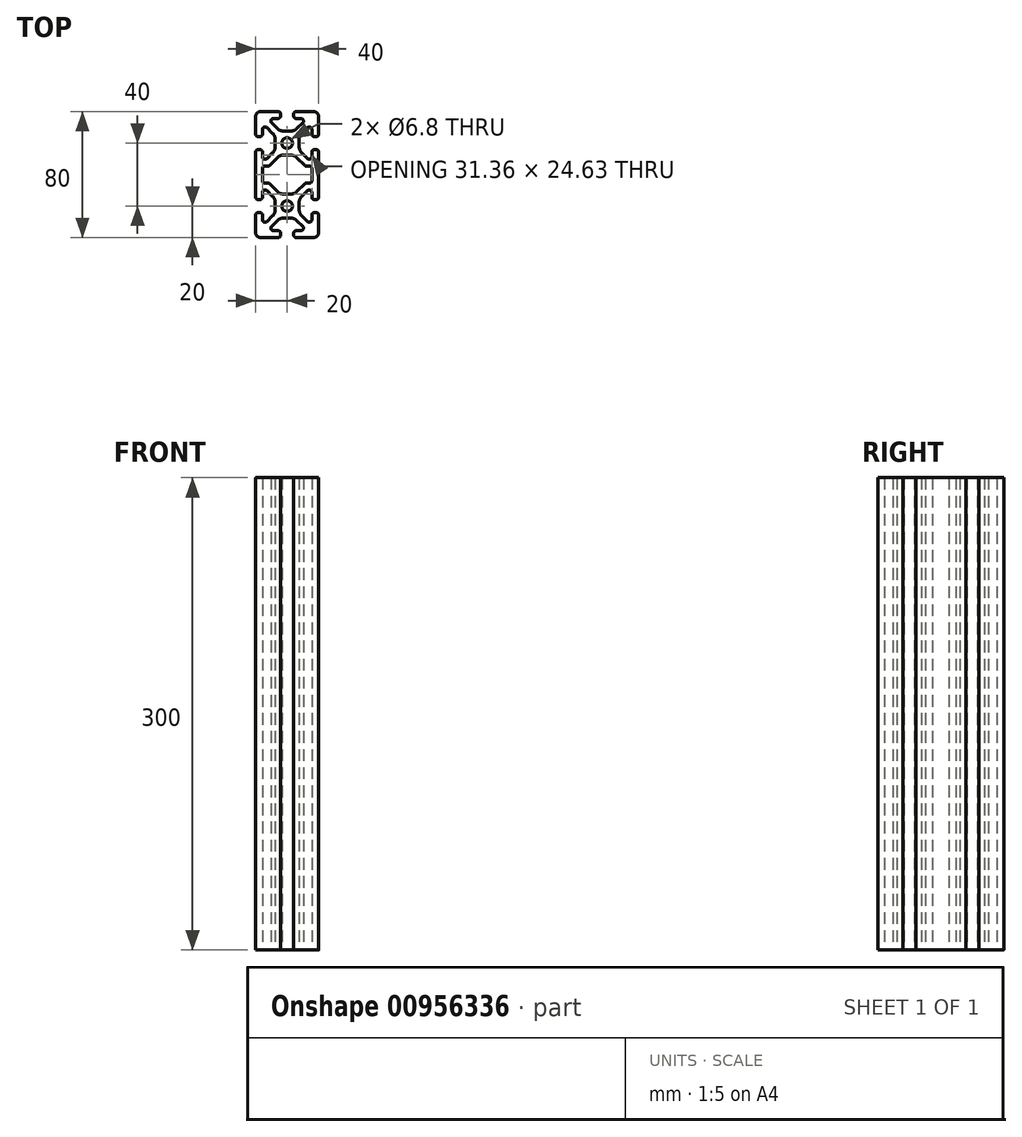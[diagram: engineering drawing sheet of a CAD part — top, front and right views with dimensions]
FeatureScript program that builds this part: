
annotation { "Feature Type Name" : "Feature", "Feature Type Description" : "" }
export const myFeature = defineFeature(function(context is Context, id is Id, definition is map)
    precondition{}
    {
        {
            assignVariable(context, id + "F0", {"name" : "height", "anyValue" : 300});
        }
        {
            var Q0;
            Q0=qCreatedBy(makeId("Top.planeOp"),FACE);
            var sketch = newSketch(context, id + "F1", { "sketchPlane" : qUnion([Q0])});
            skLineSegment(sketch, "E0", {"start": v(15.68, -4.07) * mm, "end": v(15.68, 4.07) * mm});
            skArc(sketch, "E1", {"start": v(14.4, -5.34) * mm, "mid": v(15.3, -4.97) * mm, "end": v(15.68, -4.07) * mm});
            skLineSegment(sketch, "E2", {"start": v(12.13, -5.34) * mm, "end": v(14.4, -5.34) * mm});
            skArc(sketch, "E3", {"start": v(12.13, -5.34) * mm, "mid": v(11.64, -5.44) * mm, "end": v(11.23, -5.71) * mm});
            skLineSegment(sketch, "E4", {"start": v(6.06, -10.9) * mm, "end": v(11.23, -5.71) * mm});
            skArc(sketch, "E5", {"start": v(2.62, -12.31) * mm, "mid": v(4.48, -11.94) * mm, "end": v(6.06, -10.9) * mm});
            skLineSegment(sketch, "E6", {"start": v(-2.62, -12.31) * mm, "end": v(2.62, -12.31) * mm});
            skArc(sketch, "E7", {"start": v(-6.06, -10.9) * mm, "mid": v(-4.48, -11.94) * mm, "end": v(-2.62, -12.31) * mm});
            skLineSegment(sketch, "E8", {"start": v(-11.23, -5.71) * mm, "end": v(-6.06, -10.9) * mm});
            skArc(sketch, "E9", {"start": v(-11.23, -5.71) * mm, "mid": v(-11.64, -5.44) * mm, "end": v(-12.13, -5.34) * mm});
            skLineSegment(sketch, "E10", {"start": v(-14.4, -5.34) * mm, "end": v(-12.13, -5.34) * mm});
            skArc(sketch, "E11", {"start": v(-15.68, -4.07) * mm, "mid": v(-15.3, -4.97) * mm, "end": v(-14.4, -5.34) * mm});
            skLineSegment(sketch, "E12", {"start": v(-15.68, 4.07) * mm, "end": v(-15.68, -4.07) * mm});
            skArc(sketch, "E13", {"start": v(-14.4, 5.34) * mm, "mid": v(-15.3, 4.97) * mm, "end": v(-15.68, 4.07) * mm});
            skLineSegment(sketch, "E14", {"start": v(-12.13, 5.34) * mm, "end": v(-14.4, 5.34) * mm});
            skArc(sketch, "E15", {"start": v(-12.13, 5.34) * mm, "mid": v(-11.64, 5.44) * mm, "end": v(-11.23, 5.71) * mm});
            skLineSegment(sketch, "E16", {"start": v(-6.06, 10.9) * mm, "end": v(-11.23, 5.71) * mm});
            skArc(sketch, "E17", {"start": v(-2.62, 12.32) * mm, "mid": v(-4.48, 11.94) * mm, "end": v(-6.06, 10.9) * mm});
            skLineSegment(sketch, "E18", {"start": v(2.62, 12.32) * mm, "end": v(-2.62, 12.32) * mm});
            skArc(sketch, "E19", {"start": v(6.06, 10.9) * mm, "mid": v(4.48, 11.94) * mm, "end": v(2.62, 12.32) * mm});
            skLineSegment(sketch, "E20", {"start": v(11.23, 5.71) * mm, "end": v(6.06, 10.9) * mm});
            skArc(sketch, "E21", {"start": v(11.23, 5.71) * mm, "mid": v(11.64, 5.44) * mm, "end": v(12.13, 5.34) * mm});
            skLineSegment(sketch, "E22", {"start": v(14.4, 5.34) * mm, "end": v(12.13, 5.34) * mm});
            skArc(sketch, "E23", {"start": v(15.68, 4.07) * mm, "mid": v(15.3, 4.97) * mm, "end": v(14.4, 5.34) * mm});
            skCircle(sketch, "E24", {"center": v(0, -20) * mm, "radius": 3.4 * mm});
            skCircle(sketch, "E25", {"center": v(0, 20) * mm, "radius": 3.4 * mm});
            skArc(sketch, "E26", {"start": v(16.83, -40) * mm, "mid": v(19.07, -39.07) * mm, "end": v(20, -36.83) * mm});
            skLineSegment(sketch, "E27", {"start": v(20, -36.83) * mm, "end": v(20, -25.7) * mm});
            skArc(sketch, "E28", {"start": v(20, -25.7) * mm, "mid": v(19.54, -24.58) * mm, "end": v(18.43, -24.12) * mm});
            skLineSegment(sketch, "E29", {"start": v(18.43, -24.12) * mm, "end": v(17.25, -24.12) * mm});
            skArc(sketch, "E30", {"start": v(17.25, -24.12) * mm, "mid": v(16.14, -24.58) * mm, "end": v(15.68, -25.7) * mm});
            skLineSegment(sketch, "E31", {"start": v(15.68, -25.7) * mm, "end": v(15.68, -28.72) * mm});
            skArc(sketch, "E32", {"start": v(14.1, -30.29) * mm, "mid": v(15.22, -29.83) * mm, "end": v(15.68, -28.72) * mm});
            skLineSegment(sketch, "E33", {"start": v(14.1, -30.29) * mm, "end": v(13.65, -30.29) * mm});
            skArc(sketch, "E34", {"start": v(13.12, -30.06) * mm, "mid": v(13.36, -30.23) * mm, "end": v(13.65, -30.29) * mm});
            skLineSegment(sketch, "E35", {"start": v(13.12, -30.06) * mm, "end": v(9.1, -26.06) * mm});
            skArc(sketch, "E36", {"start": v(7.68, -22.62) * mm, "mid": v(8.06, -24.48) * mm, "end": v(9.1, -26.06) * mm});
            skLineSegment(sketch, "E37", {"start": v(7.68, -22.62) * mm, "end": v(7.68, -17.38) * mm});
            skArc(sketch, "E38", {"start": v(9.1, -13.94) * mm, "mid": v(8.06, -15.52) * mm, "end": v(7.68, -17.38) * mm});
            skLineSegment(sketch, "E39", {"start": v(9.1, -13.94) * mm, "end": v(13.12, -9.94) * mm});
            skArc(sketch, "E40", {"start": v(13.65, -9.71) * mm, "mid": v(13.36, -9.77) * mm, "end": v(13.12, -9.94) * mm});
            skLineSegment(sketch, "E41", {"start": v(13.65, -9.71) * mm, "end": v(14.1, -9.71) * mm});
            skArc(sketch, "E42", {"start": v(15.68, -11.28) * mm, "mid": v(15.22, -10.17) * mm, "end": v(14.1, -9.71) * mm});
            skLineSegment(sketch, "E43", {"start": v(15.68, -11.28) * mm, "end": v(15.68, -14.3) * mm});
            skArc(sketch, "E44", {"start": v(15.68, -14.3) * mm, "mid": v(16.14, -15.42) * mm, "end": v(17.25, -15.88) * mm});
            skLineSegment(sketch, "E45", {"start": v(17.25, -15.88) * mm, "end": v(18.43, -15.88) * mm});
            skArc(sketch, "E46", {"start": v(18.43, -15.88) * mm, "mid": v(19.54, -15.42) * mm, "end": v(20, -14.3) * mm});
            skLineSegment(sketch, "E47", {"start": v(20, -14.3) * mm, "end": v(20, 14.3) * mm});
            skArc(sketch, "E48", {"start": v(20, 14.3) * mm, "mid": v(19.54, 15.42) * mm, "end": v(18.43, 15.88) * mm});
            skLineSegment(sketch, "E49", {"start": v(18.43, 15.88) * mm, "end": v(17.25, 15.88) * mm});
            skArc(sketch, "E50", {"start": v(17.25, 15.88) * mm, "mid": v(16.14, 15.42) * mm, "end": v(15.68, 14.3) * mm});
            skLineSegment(sketch, "E51", {"start": v(15.68, 14.3) * mm, "end": v(15.68, 11.28) * mm});
            skArc(sketch, "E52", {"start": v(14.1, 9.71) * mm, "mid": v(15.22, 10.17) * mm, "end": v(15.68, 11.28) * mm});
            skLineSegment(sketch, "E53", {"start": v(14.1, 9.71) * mm, "end": v(13.65, 9.71) * mm});
            skArc(sketch, "E54", {"start": v(13.12, 9.94) * mm, "mid": v(13.36, 9.77) * mm, "end": v(13.65, 9.71) * mm});
            skLineSegment(sketch, "E55", {"start": v(13.12, 9.94) * mm, "end": v(9.1, 13.94) * mm});
            skArc(sketch, "E56", {"start": v(7.68, 17.38) * mm, "mid": v(8.06, 15.52) * mm, "end": v(9.1, 13.94) * mm});
            skLineSegment(sketch, "E57", {"start": v(7.68, 17.38) * mm, "end": v(7.68, 22.62) * mm});
            skArc(sketch, "E58", {"start": v(9.1, 26.06) * mm, "mid": v(8.06, 24.48) * mm, "end": v(7.68, 22.62) * mm});
            skLineSegment(sketch, "E59", {"start": v(9.1, 26.06) * mm, "end": v(13.12, 30.06) * mm});
            skArc(sketch, "E60", {"start": v(13.65, 30.29) * mm, "mid": v(13.36, 30.23) * mm, "end": v(13.12, 30.06) * mm});
            skLineSegment(sketch, "E61", {"start": v(13.65, 30.29) * mm, "end": v(14.1, 30.29) * mm});
            skArc(sketch, "E62", {"start": v(15.68, 28.72) * mm, "mid": v(15.22, 29.83) * mm, "end": v(14.1, 30.29) * mm});
            skLineSegment(sketch, "E63", {"start": v(15.68, 28.72) * mm, "end": v(15.68, 25.7) * mm});
            skArc(sketch, "E64", {"start": v(15.68, 25.7) * mm, "mid": v(16.14, 24.58) * mm, "end": v(17.25, 24.12) * mm});
            skLineSegment(sketch, "E65", {"start": v(17.25, 24.12) * mm, "end": v(18.43, 24.12) * mm});
            skArc(sketch, "E66", {"start": v(18.43, 24.12) * mm, "mid": v(19.54, 24.58) * mm, "end": v(20, 25.7) * mm});
            skLineSegment(sketch, "E67", {"start": v(20, 25.7) * mm, "end": v(20, 36.83) * mm});
            skArc(sketch, "E68", {"start": v(20, 36.83) * mm, "mid": v(19.07, 39.07) * mm, "end": v(16.83, 40) * mm});
            skLineSegment(sketch, "E69", {"start": v(16.83, 40) * mm, "end": v(5.7, 40) * mm});
            skArc(sketch, "E70", {"start": v(5.7, 40) * mm, "mid": v(4.58, 39.54) * mm, "end": v(4.12, 38.43) * mm});
            skLineSegment(sketch, "E71", {"start": v(4.12, 38.43) * mm, "end": v(4.12, 37.25) * mm});
            skArc(sketch, "E72", {"start": v(4.12, 37.25) * mm, "mid": v(4.58, 36.14) * mm, "end": v(5.7, 35.68) * mm});
            skLineSegment(sketch, "E73", {"start": v(5.7, 35.68) * mm, "end": v(8.72, 35.68) * mm});
            skArc(sketch, "E74", {"start": v(10.29, 34.1) * mm, "mid": v(9.83, 35.22) * mm, "end": v(8.72, 35.68) * mm});
            skLineSegment(sketch, "E75", {"start": v(10.29, 34.1) * mm, "end": v(10.29, 33.65) * mm});
            skArc(sketch, "E76", {"start": v(10.06, 33.12) * mm, "mid": v(10.23, 33.36) * mm, "end": v(10.29, 33.65) * mm});
            skLineSegment(sketch, "E77", {"start": v(10.06, 33.12) * mm, "end": v(6.06, 29.1) * mm});
            skArc(sketch, "E78", {"start": v(2.62, 27.69) * mm, "mid": v(4.48, 28.06) * mm, "end": v(6.06, 29.1) * mm});
            skLineSegment(sketch, "E79", {"start": v(2.62, 27.68) * mm, "end": v(-2.62, 27.68) * mm});
            skArc(sketch, "E80", {"start": v(-6.06, 29.1) * mm, "mid": v(-4.48, 28.06) * mm, "end": v(-2.62, 27.69) * mm});
            skLineSegment(sketch, "E81", {"start": v(-6.06, 29.1) * mm, "end": v(-10.06, 33.12) * mm});
            skArc(sketch, "E82", {"start": v(-10.29, 33.65) * mm, "mid": v(-10.23, 33.36) * mm, "end": v(-10.06, 33.12) * mm});
            skLineSegment(sketch, "E83", {"start": v(-10.29, 33.65) * mm, "end": v(-10.29, 34.1) * mm});
            skArc(sketch, "E84", {"start": v(-8.72, 35.68) * mm, "mid": v(-9.83, 35.22) * mm, "end": v(-10.29, 34.1) * mm});
            skLineSegment(sketch, "E85", {"start": v(-8.72, 35.68) * mm, "end": v(-5.7, 35.68) * mm});
            skArc(sketch, "E86", {"start": v(-5.7, 35.68) * mm, "mid": v(-4.58, 36.14) * mm, "end": v(-4.12, 37.25) * mm});
            skLineSegment(sketch, "E87", {"start": v(-4.12, 37.25) * mm, "end": v(-4.12, 38.43) * mm});
            skArc(sketch, "E88", {"start": v(-4.12, 38.43) * mm, "mid": v(-4.58, 39.54) * mm, "end": v(-5.7, 40) * mm});
            skLineSegment(sketch, "E89", {"start": v(-5.7, 40) * mm, "end": v(-16.83, 40) * mm});
            skArc(sketch, "E90", {"start": v(-16.83, 40) * mm, "mid": v(-19.07, 39.07) * mm, "end": v(-20, 36.83) * mm});
            skLineSegment(sketch, "E91", {"start": v(-20, 36.83) * mm, "end": v(-20, 25.7) * mm});
            skArc(sketch, "E92", {"start": v(-20, 25.7) * mm, "mid": v(-19.54, 24.58) * mm, "end": v(-18.43, 24.12) * mm});
            skLineSegment(sketch, "E93", {"start": v(-18.43, 24.12) * mm, "end": v(-17.25, 24.12) * mm});
            skArc(sketch, "E94", {"start": v(-17.25, 24.12) * mm, "mid": v(-16.14, 24.58) * mm, "end": v(-15.68, 25.7) * mm});
            skLineSegment(sketch, "E95", {"start": v(-15.68, 25.7) * mm, "end": v(-15.68, 28.72) * mm});
            skArc(sketch, "E96", {"start": v(-14.1, 30.29) * mm, "mid": v(-15.22, 29.83) * mm, "end": v(-15.68, 28.72) * mm});
            skLineSegment(sketch, "E97", {"start": v(-14.1, 30.29) * mm, "end": v(-13.65, 30.29) * mm});
            skArc(sketch, "E98", {"start": v(-13.12, 30.06) * mm, "mid": v(-13.36, 30.23) * mm, "end": v(-13.65, 30.29) * mm});
            skLineSegment(sketch, "E99", {"start": v(-13.12, 30.06) * mm, "end": v(-9.1, 26.06) * mm});
            skArc(sketch, "E100", {"start": v(-7.68, 22.62) * mm, "mid": v(-8.06, 24.48) * mm, "end": v(-9.1, 26.06) * mm});
            skLineSegment(sketch, "E101", {"start": v(-7.68, 22.62) * mm, "end": v(-7.68, 17.38) * mm});
            skArc(sketch, "E102", {"start": v(-9.1, 13.94) * mm, "mid": v(-8.06, 15.52) * mm, "end": v(-7.68, 17.38) * mm});
            skLineSegment(sketch, "E103", {"start": v(-9.1, 13.94) * mm, "end": v(-13.12, 9.94) * mm});
            skArc(sketch, "E104", {"start": v(-13.65, 9.71) * mm, "mid": v(-13.36, 9.77) * mm, "end": v(-13.12, 9.94) * mm});
            skLineSegment(sketch, "E105", {"start": v(-13.65, 9.71) * mm, "end": v(-14.1, 9.71) * mm});
            skArc(sketch, "E106", {"start": v(-15.68, 11.28) * mm, "mid": v(-15.22, 10.17) * mm, "end": v(-14.1, 9.71) * mm});
            skLineSegment(sketch, "E107", {"start": v(-15.68, 11.28) * mm, "end": v(-15.68, 14.3) * mm});
            skArc(sketch, "E108", {"start": v(-15.68, 14.3) * mm, "mid": v(-16.14, 15.42) * mm, "end": v(-17.25, 15.88) * mm});
            skLineSegment(sketch, "E109", {"start": v(-17.25, 15.88) * mm, "end": v(-18.43, 15.88) * mm});
            skArc(sketch, "E110", {"start": v(-18.43, 15.88) * mm, "mid": v(-19.54, 15.42) * mm, "end": v(-20, 14.3) * mm});
            skLineSegment(sketch, "E111", {"start": v(-20, 14.3) * mm, "end": v(-20, -14.3) * mm});
            skArc(sketch, "E112", {"start": v(-20, -14.3) * mm, "mid": v(-19.54, -15.42) * mm, "end": v(-18.43, -15.88) * mm});
            skLineSegment(sketch, "E113", {"start": v(-18.43, -15.88) * mm, "end": v(-17.25, -15.88) * mm});
            skArc(sketch, "E114", {"start": v(-17.25, -15.88) * mm, "mid": v(-16.14, -15.42) * mm, "end": v(-15.68, -14.3) * mm});
            skLineSegment(sketch, "E115", {"start": v(-15.68, -14.3) * mm, "end": v(-15.68, -11.28) * mm});
            skArc(sketch, "E116", {"start": v(-14.1, -9.71) * mm, "mid": v(-15.22, -10.17) * mm, "end": v(-15.68, -11.28) * mm});
            skLineSegment(sketch, "E117", {"start": v(-14.1, -9.71) * mm, "end": v(-13.65, -9.71) * mm});
            skArc(sketch, "E118", {"start": v(-13.12, -9.94) * mm, "mid": v(-13.36, -9.77) * mm, "end": v(-13.65, -9.71) * mm});
            skLineSegment(sketch, "E119", {"start": v(-13.12, -9.94) * mm, "end": v(-9.1, -13.94) * mm});
            skArc(sketch, "E120", {"start": v(-7.68, -17.38) * mm, "mid": v(-8.06, -15.52) * mm, "end": v(-9.1, -13.94) * mm});
            skLineSegment(sketch, "E121", {"start": v(-7.68, -17.38) * mm, "end": v(-7.68, -22.62) * mm});
            skArc(sketch, "E122", {"start": v(-9.1, -26.06) * mm, "mid": v(-8.06, -24.48) * mm, "end": v(-7.68, -22.62) * mm});
            skLineSegment(sketch, "E123", {"start": v(-9.1, -26.06) * mm, "end": v(-13.12, -30.06) * mm});
            skArc(sketch, "E124", {"start": v(-13.65, -30.29) * mm, "mid": v(-13.36, -30.23) * mm, "end": v(-13.12, -30.06) * mm});
            skLineSegment(sketch, "E125", {"start": v(-13.65, -30.29) * mm, "end": v(-14.1, -30.29) * mm});
            skArc(sketch, "E126", {"start": v(-15.68, -28.72) * mm, "mid": v(-15.22, -29.83) * mm, "end": v(-14.1, -30.29) * mm});
            skLineSegment(sketch, "E127", {"start": v(-15.68, -28.72) * mm, "end": v(-15.68, -25.7) * mm});
            skArc(sketch, "E128", {"start": v(-15.68, -25.7) * mm, "mid": v(-16.14, -24.58) * mm, "end": v(-17.25, -24.12) * mm});
            skLineSegment(sketch, "E129", {"start": v(-17.25, -24.12) * mm, "end": v(-18.43, -24.12) * mm});
            skArc(sketch, "E130", {"start": v(-18.43, -24.12) * mm, "mid": v(-19.54, -24.58) * mm, "end": v(-20, -25.7) * mm});
            skLineSegment(sketch, "E131", {"start": v(-20, -25.7) * mm, "end": v(-20, -36.83) * mm});
            skArc(sketch, "E132", {"start": v(-20, -36.83) * mm, "mid": v(-19.07, -39.07) * mm, "end": v(-16.83, -40) * mm});
            skLineSegment(sketch, "E133", {"start": v(-16.83, -40) * mm, "end": v(-5.7, -40) * mm});
            skArc(sketch, "E134", {"start": v(-5.7, -40) * mm, "mid": v(-4.58, -39.54) * mm, "end": v(-4.12, -38.43) * mm});
            skLineSegment(sketch, "E135", {"start": v(-4.12, -38.43) * mm, "end": v(-4.12, -37.25) * mm});
            skArc(sketch, "E136", {"start": v(-4.12, -37.25) * mm, "mid": v(-4.58, -36.14) * mm, "end": v(-5.7, -35.68) * mm});
            skLineSegment(sketch, "E137", {"start": v(-5.7, -35.68) * mm, "end": v(-8.72, -35.68) * mm});
            skArc(sketch, "E138", {"start": v(-10.29, -34.1) * mm, "mid": v(-9.83, -35.22) * mm, "end": v(-8.72, -35.68) * mm});
            skLineSegment(sketch, "E139", {"start": v(-10.29, -34.1) * mm, "end": v(-10.29, -33.65) * mm});
            skArc(sketch, "E140", {"start": v(-10.06, -33.12) * mm, "mid": v(-10.23, -33.36) * mm, "end": v(-10.29, -33.65) * mm});
            skLineSegment(sketch, "E141", {"start": v(-10.06, -33.12) * mm, "end": v(-6.06, -29.1) * mm});
            skArc(sketch, "E142", {"start": v(-2.62, -27.69) * mm, "mid": v(-4.48, -28.06) * mm, "end": v(-6.06, -29.1) * mm});
            skLineSegment(sketch, "E143", {"start": v(-2.62, -27.69) * mm, "end": v(2.62, -27.69) * mm});
            skArc(sketch, "E144", {"start": v(6.06, -29.1) * mm, "mid": v(4.48, -28.06) * mm, "end": v(2.62, -27.69) * mm});
            skLineSegment(sketch, "E145", {"start": v(6.06, -29.1) * mm, "end": v(10.06, -33.12) * mm});
            skArc(sketch, "E146", {"start": v(10.29, -33.65) * mm, "mid": v(10.23, -33.36) * mm, "end": v(10.06, -33.12) * mm});
            skLineSegment(sketch, "E147", {"start": v(10.29, -33.65) * mm, "end": v(10.29, -34.1) * mm});
            skArc(sketch, "E148", {"start": v(8.72, -35.68) * mm, "mid": v(9.83, -35.22) * mm, "end": v(10.29, -34.1) * mm});
            skLineSegment(sketch, "E149", {"start": v(8.72, -35.68) * mm, "end": v(5.7, -35.68) * mm});
            skArc(sketch, "E150", {"start": v(5.7, -35.68) * mm, "mid": v(4.58, -36.14) * mm, "end": v(4.12, -37.25) * mm});
            skLineSegment(sketch, "E151", {"start": v(4.12, -37.25) * mm, "end": v(4.12, -38.43) * mm});
            skArc(sketch, "E152", {"start": v(4.12, -38.43) * mm, "mid": v(4.58, -39.54) * mm, "end": v(5.7, -40) * mm});
            skLineSegment(sketch, "E153", {"start": v(5.7, -40) * mm, "end": v(16.83, -40) * mm});
            skSolve(sketch);
        }
        {
            var Q0;
            Q0=makeQuery(id+"F1.imprint","IMPRINT",FACE,{"disambiguationData":[TD([[makeQuery(id+"F1.imprint","IMPRINT",EDGE,{"derivedFrom":sQuery(id+"F1.wireOp",EDGE,"E0")}),-1.0]])]});
            extrude(context, id + "F2", {"entities" : qUnion([Q0]), "depth" : (getVariable(context, 'height')) * mm, "offsetDistance" : 25 * mm});
        }
    });
